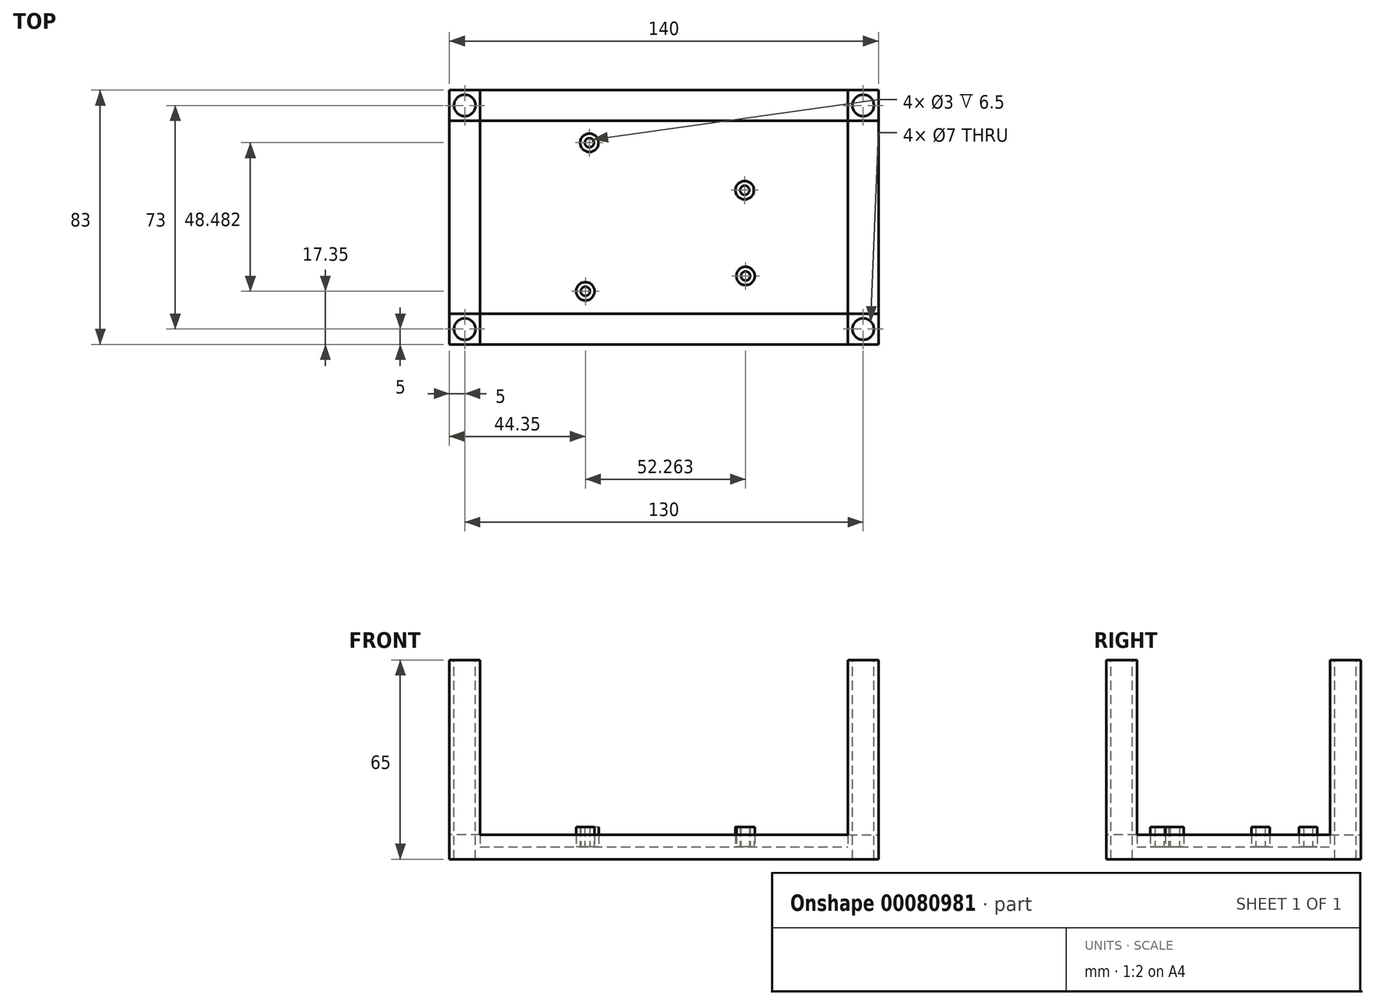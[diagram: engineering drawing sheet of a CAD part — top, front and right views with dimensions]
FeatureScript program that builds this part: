
annotation { "Feature Type Name" : "Feature", "Feature Type Description" : "" }
export const myFeature = defineFeature(function(context is Context, id is Id, definition is map)
    precondition{}
    {
        {
            var Q0;
            Q0=qCreatedBy(makeId("Top.planeOp"),FACE);
            var sketch = newSketch(context, id + "F0", { "sketchPlane" : qUnion([Q0])});
            skLineSegment(sketch, "E0.bottom", {"start": v(-70, 50) * mm, "end": v(70, 50) * mm, "construction": true});
            skLineSegment(sketch, "E0.top", {"start": v(-70, -50) * mm, "end": v(70, -50) * mm, "construction": true});
            skLineSegment(sketch, "E0.left", {"start": v(-70, 50) * mm, "end": v(-70, -50) * mm, "construction": true});
            skLineSegment(sketch, "E0.right", {"start": v(70, 50) * mm, "end": v(70, -50) * mm, "construction": true});
            skPoint(sketch, "E0.middle", {"position": v(0, 0) * mm});
            skLineSegment(sketch, "E1", {"start": v(-70, 50) * mm, "end": v(-70, 33) * mm});
            skLineSegment(sketch, "E2.bottom", {"start": v(-70, 33) * mm, "end": v(-60, 33) * mm});
            skLineSegment(sketch, "E2.top", {"start": v(-70, 23) * mm, "end": v(-60, 23) * mm});
            skLineSegment(sketch, "E2.left", {"start": v(-70, 33) * mm, "end": v(-70, 23) * mm});
            skLineSegment(sketch, "E2.right", {"start": v(-60, 33) * mm, "end": v(-60, 23) * mm});
            skLineSegment(sketch, "E3", {"start": v(70, 50) * mm, "end": v(70, 33) * mm});
            skLineSegment(sketch, "E4.bottom", {"start": v(70, 33) * mm, "end": v(60, 33) * mm});
            skLineSegment(sketch, "E4.top", {"start": v(70, 23) * mm, "end": v(60, 23) * mm});
            skLineSegment(sketch, "E4.left", {"start": v(70, 33) * mm, "end": v(70, 23) * mm});
            skLineSegment(sketch, "E4.right", {"start": v(60, 33) * mm, "end": v(60, 23) * mm});
            skLineSegment(sketch, "E5.bottom", {"start": v(-70, -50) * mm, "end": v(-60, -50) * mm});
            skLineSegment(sketch, "E5.top", {"start": v(-70, -40) * mm, "end": v(-60, -40) * mm});
            skLineSegment(sketch, "E5.left", {"start": v(-70, -50) * mm, "end": v(-70, -40) * mm});
            skLineSegment(sketch, "E5.right", {"start": v(-60, -50) * mm, "end": v(-60, -40) * mm});
            skLineSegment(sketch, "E6.bottom", {"start": v(70, -50) * mm, "end": v(60, -50) * mm});
            skLineSegment(sketch, "E6.top", {"start": v(70, -40) * mm, "end": v(60, -40) * mm});
            skLineSegment(sketch, "E6.left", {"start": v(70, -50) * mm, "end": v(70, -40) * mm});
            skLineSegment(sketch, "E6.right", {"start": v(60, -50) * mm, "end": v(60, -40) * mm});
            skSolve(sketch);
        }
        {
            var Q0;
            Q0=qSketchRegion(id+"F0",true);
            extrude(context, id + "F1", {"entities" : qUnion([Q0]), "oppositeDirection" : true, "depth" : 65 * mm});
        }
        {
            var Q0;
            Q0=qCreatedBy(makeId("Top.planeOp"),FACE);
            cPlane(context, id + "F2", {"entities" : qUnion([Q0]), "cplaneType" : CPlaneType.OFFSET, "offset" : 65 * mm, "oppositeDirection" : true, "width" : 150 * mm, "height" : 150 * mm});
        }
        {
            var Q0;
            Q0=qCreatedBy(id+"F2.planeOp",FACE);
            var sketch = newSketch(context, id + "F3", { "sketchPlane" : qUnion([Q0])});
            skLineSegment(sketch, "E7.0", {"start": v(-70, -50) * mm, "end": v(-70, -40) * mm});
            skLineSegment(sketch, "E8.0", {"start": v(-70, -50) * mm, "end": v(-60, -50) * mm});
            skLineSegment(sketch, "E9.0", {"start": v(70, -50) * mm, "end": v(60, -50) * mm});
            skLineSegment(sketch, "E10.0", {"start": v(70, -50) * mm, "end": v(70, -40) * mm});
            skLineSegment(sketch, "E11.0.0", {"start": v(-70, -40) * mm, "end": v(-70, -50) * mm});
            skLineSegment(sketch, "E12.0.0", {"start": v(60, -50) * mm, "end": v(70, -50) * mm});
            skLineSegment(sketch, "E13", {"start": v(-60, -50) * mm, "end": v(60, -50) * mm});
            skLineSegment(sketch, "E14", {"start": v(70, -40) * mm, "end": v(70, 23) * mm});
            skLineSegment(sketch, "E15", {"start": v(-60, 23) * mm, "end": v(60, 23) * mm});
            skLineSegment(sketch, "E16", {"start": v(60, -40) * mm, "end": v(60, 23) * mm});
            skLineSegment(sketch, "E17", {"start": v(60, -40) * mm, "end": v(-60, -40) * mm});
            skLineSegment(sketch, "E18", {"start": v(-60, -40) * mm, "end": v(-60, 23) * mm});
            skLineSegment(sketch, "E19", {"start": v(-70, 23) * mm, "end": v(-70, -40) * mm});
            skPoint(sketch, "E20.0.2.end.orphan", {"position": v(60, 23) * mm});
            skPoint(sketch, "E21.0", {"position": v(-70, 33) * mm});
            skLineSegment(sketch, "E22.bottom", {"start": v(-70, 33) * mm, "end": v(70, 33) * mm});
            skLineSegment(sketch, "E22.top", {"start": v(-70, 23) * mm, "end": v(70, 23) * mm});
            skLineSegment(sketch, "E22.left", {"start": v(-70, 33) * mm, "end": v(-70, 23) * mm});
            skLineSegment(sketch, "E22.right", {"start": v(70, 33) * mm, "end": v(70, 23) * mm});
            skSolve(sketch);
        }
        {
            var Q0;
            Q0=qSketchRegion(id+"F3",true);
            extrude(context, id + "F4", {"entities" : qUnion([Q0]), "operationType" : NewBodyOperationType.ADD, "depth" : 8 * mm});
        }
        {
            var Q0;
            Q0=qCreatedBy(id+"F2.planeOp",FACE);
            var sketch = newSketch(context, id + "F5", { "sketchPlane" : qUnion([Q0])});
            skPoint(sketch, "E23.0", {"position": v(-70, 33) * mm});
            skPoint(sketch, "E24.0", {"position": v(70, -50) * mm});
            skLineSegment(sketch, "E25.bottom", {"start": v(-70, 33) * mm, "end": v(70, 33) * mm});
            skLineSegment(sketch, "E25.top", {"start": v(-70, -50) * mm, "end": v(70, -50) * mm});
            skLineSegment(sketch, "E25.left", {"start": v(-70, 33) * mm, "end": v(-70, -50) * mm});
            skLineSegment(sketch, "E25.right", {"start": v(70, 33) * mm, "end": v(70, -50) * mm});
            skSolve(sketch);
        }
        {
            var Q0;
            Q0=qSketchRegion(id+"F5",true);
            extrude(context, id + "F6", {"entities" : qUnion([Q0]), "operationType" : NewBodyOperationType.ADD, "depth" : 4 * mm});
        }
        {
            var Q0;
            Q0=qCreatedBy(id+"F2.planeOp",FACE);
            var sketch = newSketch(context, id + "F7", { "sketchPlane" : qUnion([Q0])});
            skLineSegment(sketch, "E26", {"start": v(-24.36, -18.42) * mm, "end": v(-24.36, -17.12) * mm, "construction": true});
            skPoint(sketch, "E27.middle", {"position": v(0, -8.5) * mm});
            skCircle(sketch, "E28", {"center": v(-24.35, 15.83) * mm, "radius": 1.5 * mm});
            skCircle(sketch, "E29", {"center": v(-25.65, -32.65) * mm, "radius": 1.5 * mm});
            skCircle(sketch, "E30", {"center": v(26.34, 0.33) * mm, "radius": 1.5 * mm});
            skCircle(sketch, "E31", {"center": v(26.61, -27.67) * mm, "radius": 1.5 * mm});
            skCircle(sketch, "E32", {"center": v(-24.35, 15.83) * mm, "radius": 3 * mm});
            skCircle(sketch, "E33", {"center": v(26.34, 0.33) * mm, "radius": 3 * mm});
            skCircle(sketch, "E34", {"center": v(26.61, -27.67) * mm, "radius": 3 * mm});
            skCircle(sketch, "E35", {"center": v(-25.65, -32.65) * mm, "radius": 3 * mm});
            skLineSegment(sketch, "E36", {"start": v(-24.35, 15.83) * mm, "end": v(26.34, 0.33) * mm, "construction": true});
            skLineSegment(sketch, "E37", {"start": v(26.34, 0.33) * mm, "end": v(26.61, -27.67) * mm, "construction": true});
            skLineSegment(sketch, "E38", {"start": v(26.61, -27.67) * mm, "end": v(-25.65, -32.65) * mm, "construction": true});
            skLineSegment(sketch, "E39", {"start": v(-25.65, -32.65) * mm, "end": v(-24.35, 15.83) * mm, "construction": true});
            skLineSegment(sketch, "E40", {"start": v(-24.35, 15.83) * mm, "end": v(26.61, -27.67) * mm, "construction": true});
            skLineSegment(sketch, "E41", {"start": v(26.34, 0.33) * mm, "end": v(-25.65, -32.65) * mm, "construction": true});
            skSolve(sketch);
        }
        {
            var Q0;
            Q0=qSketchRegion(id+"F7",true);
            extrude(context, id + "F8", {"entities" : qUnion([Q0]), "operationType" : NewBodyOperationType.ADD, "depth" : 10.5 * mm});
        }
        {
            var Q0;
            Q0=qCreatedBy(makeId("Top.planeOp"),FACE);
            var sketch = newSketch(context, id + "F9", { "sketchPlane" : qUnion([Q0])});
            skLineSegment(sketch, "E42.0", {"start": v(-60, 33) * mm, "end": v(-60, 23) * mm});
            skLineSegment(sketch, "E43.0", {"start": v(-70, 23) * mm, "end": v(-60, 23) * mm});
            skLineSegment(sketch, "E44.0", {"start": v(-70, -40) * mm, "end": v(-60, -40) * mm});
            skLineSegment(sketch, "E45.0", {"start": v(-60, -50) * mm, "end": v(-60, -40) * mm});
            skLineSegment(sketch, "E46.0", {"start": v(60, -50) * mm, "end": v(60, -40) * mm});
            skLineSegment(sketch, "E47.0", {"start": v(70, -40) * mm, "end": v(60, -40) * mm});
            skLineSegment(sketch, "E48.0", {"start": v(70, 23) * mm, "end": v(60, 23) * mm});
            skLineSegment(sketch, "E49.0", {"start": v(60, 33) * mm, "end": v(60, 23) * mm});
            skCircle(sketch, "E50", {"center": v(-65, 28) * mm, "radius": 3.5 * mm});
            skPoint(sketch, "E50.centerSnap0", {"position": v(-60, 28) * mm});
            skPoint(sketch, "E50.centerSnap1", {"position": v(-65, 23) * mm});
            skCircle(sketch, "E51", {"center": v(-65, -45) * mm, "radius": 3.5 * mm});
            skPoint(sketch, "E51.centerSnap0", {"position": v(-60, -45) * mm});
            skPoint(sketch, "E51.centerSnap1", {"position": v(-65, -40) * mm});
            skCircle(sketch, "E52", {"center": v(65, -45) * mm, "radius": 3.5 * mm});
            skPoint(sketch, "E52.centerSnap0", {"position": v(60, -45) * mm});
            skPoint(sketch, "E52.centerSnap1", {"position": v(65, -40) * mm});
            skCircle(sketch, "E53", {"center": v(65, 28) * mm, "radius": 3.5 * mm});
            skPoint(sketch, "E53.centerSnap0", {"position": v(65, 23) * mm});
            skPoint(sketch, "E53.centerSnap1", {"position": v(60, 28) * mm});
            skSolve(sketch);
        }
        {
            var Q0;
            Q0 = qSketchRegion(id + "F9", true);
            extrude(context, id + "F10", {"entities" : qUnion([Q0]), "operationType" : NewBodyOperationType.REMOVE, "oppositeDirection" : true, "depth" : 70 * mm});
        }
    });
